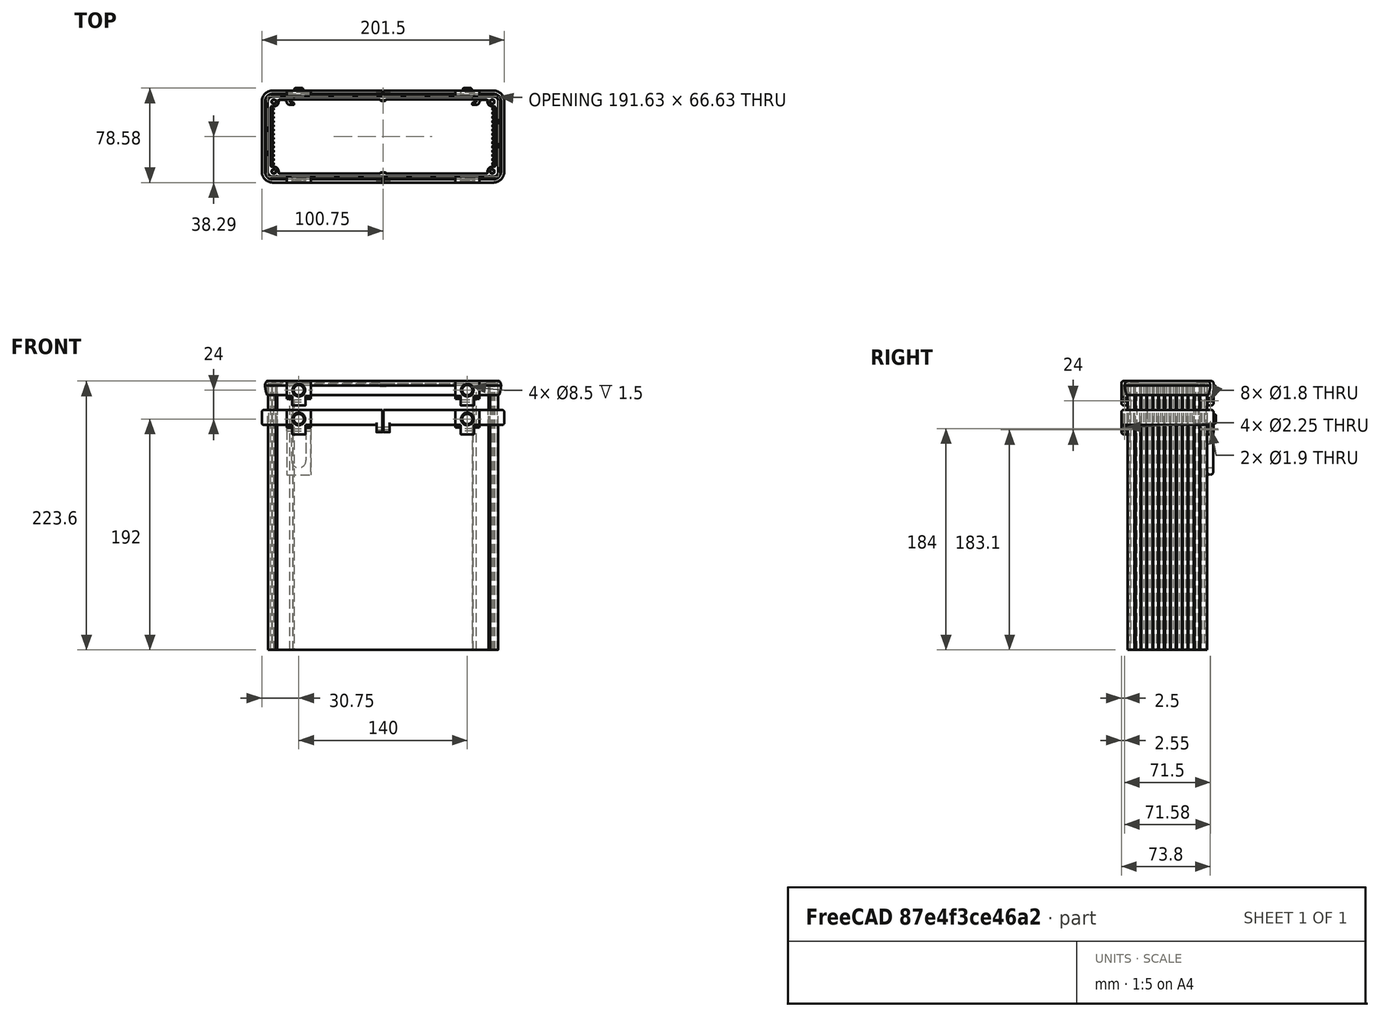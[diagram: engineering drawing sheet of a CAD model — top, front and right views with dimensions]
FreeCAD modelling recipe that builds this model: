
FCSTD DOCUMENT  (FreeCAD 1.0R38806 (Git))
Label: BevelHinge
License: All rights reserved
LicenseURL: http://en.wikipedia.org/wiki/All_rights_reserved
objects: PartDesign::Body×11, Sketcher::SketchObject×10, PartDesign::Pad×8, PartDesign::FeatureBase×6, PartDesign::Pocket×5, PartDesign::Fillet×4, Part::Feature×3, PartDesign::SubShapeBinder×3, App::Link×2, App::FeaturePython×2, Part::Compound×2, Mesh::Feature×1, Assembly::JointGroup×1, Assembly::AssemblyObject×1, PartDesign::Chamfer×1, Part::Mirroring×1
note: 106 computed .brp shape members not serialized (recipe doc carries the construction recipe); baked Part::Feature solids carry a one-line shape summary decoded from their .brp

FEATURE [Mesh::Feature] Lenovo_flip_feet_V3_2mm
FEATURE [Part::Feature] Lenovo_flip_feet_V3_2mm001
  Placement = pos=(-1.1e-15,-66.3,79.6) rot=(0,-0.707107,0.707107;3.14159rad)
  shape: bbox 20 x 5 x 43.92 mm, 906 faces, 0 solids (baked)
FEATURE [Part::Feature] Part__Feature019  label="1455U Open Bezel"
  Placement = pos=(6.2e-15,-33.01,110) rot=(0,0,1;0rad)
  shape: bbox 196.1 x 71.1 x 11.6 mm, 100 faces (baked)
FEATURE [Sketcher::SketchObject] Sketch
  ArcFitTolerance = 1e-06
  AttachmentSupport = -> [XZ_Plane]
  FullyConstrained = true
  MakeInternals = false
  MapMode = 5
  Placement = pos=(0,0,0) rot=(1,0,0;1.5708rad)
  sketch-geometry (11):
    g0: LineSegment StartX=-4.5 StartY=-1.2 StartZ=0 EndX=1.812e-13 EndY=-1.2 EndZ=0
    g1: LineSegment StartX=1.812e-13 StartY=-1.2 StartZ=0 EndX=1.812e-13 EndY=3.6 EndZ=0
    g2: LineSegment StartX=-4.5 StartY=-1.2 StartZ=0 EndX=-4.5 EndY=-6.7 EndZ=0
    g3: LineSegment StartX=-4.5 StartY=-6.7 StartZ=0 EndX=-15.5 EndY=-6.7 EndZ=0
    g4: LineSegment StartX=-15.5 StartY=-6.7 StartZ=0 EndX=-15.5 EndY=-1.2 EndZ=0
    g5: LineSegment StartX=-15.5 StartY=-1.2 StartZ=0 EndX=-20 EndY=-1.2 EndZ=0
    g6: LineSegment StartX=-20 StartY=-1.2 StartZ=0 EndX=-20 EndY=3.6 EndZ=0
    g7: ArcOfCircle [constr] CenterX=-10 CenterY=3.6 CenterZ=0 NormalX=0 NormalY=0 NormalZ=1 AngleXU=0 Radius=10 StartAngle=-2.64579e-11 EndAngle=3.14159
    g8: LineSegment StartX=-20 StartY=3.6 StartZ=0 EndX=-20 EndY=13.6 EndZ=0
    g9: LineSegment StartX=-20 StartY=13.6 StartZ=0 EndX=1.812e-13 EndY=13.6 EndZ=0
    g10: LineSegment StartX=1.812e-13 StartY=3.6 StartZ=0 EndX=1.812e-13 EndY=13.6 EndZ=0
  constraints (31):
    c: Horizontal(g0)
    c: Coincident(g0,g1)
    c: Vertical(g1)
    c: Coincident(g0,g2)
    c: Vertical(g2)
    c: Coincident(g2,g3)
    c: Horizontal(g3)
    c: Coincident(g3,g4)
    c: Vertical(g4)
    c: Coincident(g4,g5)
    c: Horizontal(g5)
    c: Coincident(g5,g6)
    c: Vertical(g6)
    c: Tangent(g7,g6) = 1.5708
    c: Tangent(g7,g1) = -1.5708
    c: DistanceX(g3,g3) = 11
    c: DistanceY(g4,g4) = 5.5
    c: Equal(g0,g5)
    c: DistanceX(g5,g5) = 4.5
    c: PointOnObject(g0,g-2)
    c: DistanceY(g0,g-1) = 1.2
    c: DistanceY(g6,g6) = 4.8
    c: Equal(g6,g1)
    c: Coincident(g8,g6)
    c: Vertical(g8)
    c: Horizontal(g9)
    c: Coincident(g10,g9)
    c: Vertical(g10)
    c: Coincident(g10,g1)
    c: Coincident(g8,g9)
    c: Tangent(g7,g9)
FEATURE [PartDesign::Pad] Pad
  Direction = (0,-1,2e-16)
  Length = 5
  Length2 = 10
  Placement = pos=(0,0,0) rot=(1,0,0;1.5708rad)
  Profile = -> Sketch
  ReferenceAxis = -> Sketch [N_Axis]
  Suppressed = false
  Type = 0
FEATURE [Sketcher::SketchObject] Sketch001
  ArcFitTolerance = 1e-06
  AttachmentSupport = -> [Pad]
  ExternalGeometry = -> [Pad]
  FullyConstrained = true
  MakeInternals = false
  MapMode = 5
  Placement = pos=(1.812e-13,0,0) rot=(0.707107,0,0.707107;3.14159rad)
  sketch-geometry (3):
    g0: LineSegment StartX=-1.2 StartY=0 StartZ=0 EndX=1 EndY=5 EndZ=0
    g1: LineSegment StartX=1 StartY=5 StartZ=0 EndX=-1.2 EndY=5 EndZ=0
    g2: LineSegment StartX=-1.2 StartY=5 StartZ=0 EndX=-1.2 EndY=0 EndZ=0
  constraints (8):
    c: Coincident(g0,g1)
    c: Horizontal(g1)
    c: Coincident(g1,g2)
    c: Vertical(g2)
    c: Coincident(g0,g2)
    c: Coincident(g0,g-3)
    c: PointOnObject(g0,g-4)
    c: DistanceX(g-1,g0) = 1
FEATURE [PartDesign::Pocket] Pocket
  BaseFeature = -> Pad
  Direction = (-1,0,2e-16)
  Length = 0
  Length2 = 5
  Placement = pos=(0,0,0) rot=(1,0,0;1.5708rad)
  Profile = -> Sketch001
  ReferenceAxis = -> Sketch001 [N_Axis]
  Suppressed = false
  Type = 3
  UpToFace = -> Pad [Face10]
FEATURE [PartDesign::SubShapeBinder] Binder
  BindCopyOnChange = 0
  BindMode = 0
  ClaimChildren = false
  Context = -> Body [Binder.]
  Fuse = false
  MakeFace = true
  OffsetFill = false
  OffsetIntersection = false
  OffsetJoinType = 0
  OffsetOpenResult = false
  PartialLoad = false
  Placement = pos=(-22,0,0) rot=(0,0,1;0rad)
  Relative = true
  Support = -> [Sketch001]
  _Version = 2
FEATURE [PartDesign::Pocket] Pocket001
  BaseFeature = -> Pocket
  Direction = (-1,0,2e-16)
  Length = 0
  Length2 = 5
  Placement = pos=(0,0,0) rot=(1,0,0;1.5708rad)
  Profile = -> Binder
  Reversed = true
  Suppressed = false
  Type = 3
  UpToFace = -> Pocket [Face7]
FEATURE [Sketcher::SketchObject] Sketch002
  ArcFitTolerance = 1e-06
  AttachmentSupport = -> [YZ_Plane]
  FullyConstrained = true
  MakeInternals = false
  MapMode = 5
  Placement = pos=(0,0,0) rot=(0.57735,0.57735,0.57735;2.0944rad)
  sketch-geometry (1):
    g0: Circle CenterX=-2.5 CenterY=-2.9 CenterZ=0 NormalX=0 NormalY=0 NormalZ=1 AngleXU=0 Radius=0.9
  constraints (3):
    c: DistanceX(g0) = -2.5
    c: DistanceY(g0) = -2.9
    c: Diameter(g0) = 1.8
FEATURE [PartDesign::Pocket] Pocket002
  BaseFeature = -> Pocket001
  Direction = (-1,0,0)
  Length = 5
  Length2 = 5
  Placement = pos=(0,0,0) rot=(1,0,0;1.5708rad)
  Profile = -> Sketch002
  ReferenceAxis = -> Sketch002 [N_Axis]
  Suppressed = false
  Type = 1
FEATURE [Sketcher::SketchObject] Sketch003
  ArcFitTolerance = 1e-06
  AttachmentSupport = -> [XZ_Plane001]
  FullyConstrained = true
  MakeInternals = false
  MapMode = 5
  Placement = pos=(0,0,0) rot=(1,0,0;1.5708rad)
  sketch-geometry (8):
    g0: LineSegment StartX=0 StartY=-0.5 StartZ=0 EndX=-4 EndY=-0.5 EndZ=0
    g1: LineSegment StartX=-4 StartY=-0.5 StartZ=0 EndX=-4 EndY=-28.5 EndZ=0
    g2: LineSegment StartX=-16 StartY=-28.5 StartZ=0 EndX=-16 EndY=-0.5 EndZ=0
    g3: LineSegment StartX=-16 StartY=-0.5 StartZ=0 EndX=-20 EndY=-0.5 EndZ=0
    g4: LineSegment StartX=-20 StartY=-0.5 StartZ=0 EndX=-20 EndY=-40.5 EndZ=0
    g5: LineSegment StartX=-20 StartY=-40.5 StartZ=0 EndX=0 EndY=-40.5 EndZ=0
    g6: LineSegment StartX=0 StartY=-40.5 StartZ=0 EndX=0 EndY=-0.5 EndZ=0
    g7: ArcOfCircle CenterX=-10 CenterY=-28.5 CenterZ=0 NormalX=0 NormalY=0 NormalZ=1 AngleXU=0 Radius=6 StartAngle=3.14159 EndAngle=6.28319
  constraints (23):
    c: Horizontal(g0)
    c: Coincident(g0,g1)
    c: Vertical(g1)
    c: Vertical(g2)
    c: Coincident(g2,g3)
    c: Horizontal(g3)
    c: Coincident(g3,g4)
    c: Vertical(g4)
    c: Coincident(g4,g5)
    c: PointOnObject(g5,g-2)
    c: Horizontal(g5)
    c: Coincident(g5,g6)
    c: Coincident(g6,g0)
    c: Vertical(g6)
    c: Tangent(g7,g1) = 1.5708
    c: Tangent(g7,g2) = 1.5708
    c: DistanceX(g3,g3) = 4
    c: Equal(g3,g0)
    c: Equal(g1,g2)
    c: DistanceY(g4,g4) = 40
    c: DistanceY(g2,g2) = 28
    c: DistanceX(g2,g0) = 12
    c: DistanceY(g0,g-1) = 0.5
FEATURE [PartDesign::Pad] Pad001
  Direction = (0,-1,2e-16)
  Length = 5
  Length2 = 10
  Placement = pos=(0,0,0) rot=(1,0,0;1.5708rad)
  Profile = -> Sketch003
  ReferenceAxis = -> Sketch003 [N_Axis]
  Suppressed = false
  Type = 0
FEATURE [Sketcher::SketchObject] Sketch004
  ArcFitTolerance = 1e-06
  AttachmentSupport = -> [YZ_Plane001]
  ExternalGeometry = -> [Pad001]
  FullyConstrained = true
  MakeInternals = false
  MapMode = 5
  Placement = pos=(0,0,0) rot=(0.57735,0.57735,0.57735;2.0944rad)
  sketch-geometry (11):
    g0: Circle CenterX=-2.5 CenterY=-2.9 CenterZ=0 NormalX=0 NormalY=0 NormalZ=1 AngleXU=0 Radius=0.95
    g1: ArcOfCircle CenterX=-2.5 CenterY=-37.8 CenterZ=0 NormalX=0 NormalY=0 NormalZ=1 AngleXU=0 Radius=2.5 StartAngle=3.14159 EndAngle=6.28319
    g2: LineSegment StartX=-5 StartY=-37.8 StartZ=0 EndX=-5 EndY=-2.4 EndZ=0
    g3: LineSegment StartX=-5 StartY=-2.4 StartZ=0 EndX=-3.1 EndY=-0.5 EndZ=0
    g4: ArcOfCircle CenterX=-3.09998 CenterY=-3.59998 CenterZ=0 NormalX=0 NormalY=0 NormalZ=1 AngleXU=0 Radius=3.09998 StartAngle=1e-16 EndAngle=1.5708
    g5: LineSegment StartX=-4e-16 StartY=-3.59998 StartZ=0 EndX=-4e-16 EndY=-37.8 EndZ=0
    g6: LineSegment [constr] StartX=-2.5 StartY=-37.8 StartZ=0 EndX=-2.5 EndY=-40.3 EndZ=0
    g7: LineSegment StartX=-10 StartY=5 StartZ=0 EndX=-10 EndY=-45 EndZ=0
    g8: LineSegment StartX=-10 StartY=-45 StartZ=0 EndX=10 EndY=-45 EndZ=0
    g9: LineSegment StartX=10 StartY=-45 StartZ=0 EndX=10 EndY=5 EndZ=0
    g10: LineSegment StartX=10 StartY=5 StartZ=0 EndX=-10 EndY=5 EndZ=0
  constraints (31):
    c: DistanceX(g0) = -2.5
    c: DistanceY(g0) = -2.9
    c: Diameter(g0) = 1.9
    c: Vertical(g2)
    c: Tangent(g2,g1) = 1.5708
    c: Coincident(g3,g4)
    c: Coincident(g3,g2)
    c: Vertical(g5)
    c: Tangent(g1,g5) = 1.5708
    c: Tangent(g5,g4) = 1.5708
    c: PointOnObject(g4,g-2)
    c: DistanceX(g2,g-1) = 5
    c: PointOnObject(g3,g-3)
    c: DistanceX(g2,g3) = 1.9
    c: Tangent(g4,g-3)
    c: Coincident(g6,g1)
    c: PointOnObject(g6,g1)
    c: Vertical(g6)
    c: DistanceY(g6) = -40.3
    c: DistanceY(g2) = -2.4
    c: Coincident(g7,g8)
    c: Coincident(g8,g9)
    c: Coincident(g9,g10)
    c: Coincident(g10,g7)
    c: Vertical(g7)
    c: Vertical(g9)
    c: Horizontal(g8)
    c: Symmetric(g7,g9,g-2)
    c: DistanceY(g7,g7) = 50
    c: DistanceX(g10,g10) = 20
    c: DistanceY(g9) = 5
FEATURE [App::Link] Body002
  LinkPlacement = pos=(3.99107,-60.6985,90.648) rot=(0,0,1;0rad)
  LinkedObject = -> Body
  Placement = pos=(3.99107,-60.6985,90.648) rot=(0,0,1;0rad)
FEATURE [App::FeaturePython] GroundedJoint  # Assembly grounded joint (typed FeaturePython)
  ObjectToGround = -> Body002
  Placement = pos=(3.99107,-60.6985,90.648) rot=(0,0,1;0rad)
FEATURE [App::Link] Body003
  LinkPlacement = pos=(1.73898,-284.407,480.336) rot=(0.999747,0.013661,0.017877;4.13204rad)
  LinkedObject = -> Body001
  Placement = pos=(1.73898,-284.407,480.336) rot=(0.999747,0.013661,0.017877;4.13204rad)
FEATURE [PartDesign::Pocket] Pocket003
  BaseFeature = -> Pad001
  Direction = (-1,0,0)
  Length = 5
  Length2 = 5
  Placement = pos=(0,0,0) rot=(1,0,0;1.5708rad)
  Profile = -> Sketch004
  ReferenceAxis = -> Sketch004 [N_Axis]
  Suppressed = false
  Type = 1
FEATURE [PartDesign::Body] Body001  label="Hinge"
  AllowCompound = false
  Group = -> [Sketch003,Pad001,Sketch004,Pocket003]
  Origin = -> Origin001
  Placement = pos=(-60,5,76) rot=(0,0,1;0rad)
  Tip = -> Pocket003
FEATURE [PartDesign::Fillet] Fillet
  Base = -> Pocket002 [Edge26,Edge20]
  BaseFeature = -> Pocket002
  Placement = pos=(0,0,0) rot=(1,0,0;1.5708rad)
  Radius = 2
  SupportTransform = false
  Suppressed = false
  UseAllEdges = false
FEATURE [App::FeaturePython] Revolute  # Assembly joint (typed FeaturePython)
  Activated = true
  AngleMax = 0
  AngleMin = -113.85
  Detach1 = false
  Detach2 = false
  Distance = 0
  Distance2 = 0
  EnableAngleMax = true
  EnableAngleMin = true
  EnableLengthMax = false
  EnableLengthMin = false
  JointType = 1 (Revolute)
  LengthMax = 0
  LengthMin = 0
  Placement1 = pos=(-2.25,-5,1) rot=(-0.707107,0,0.707107;3.14159rad)
  Placement2 = pos=(-13.8391,204.961,395.868) rot=(-0.999798,-0.012245,-0.015925;4.1597rad)
  Reference1 = -> Assembly [Body002.Fillet.Edge6,Body002.Fillet.Edge6]
  Reference2 = -> Assembly [Body003.Pocket003.?Edge31,Body003.Pocket003.?Edge31]
FEATURE [Assembly::JointGroup] Joints
  Group = -> [GroundedJoint,Revolute]
FEATURE [Assembly::AssemblyObject] Assembly
  Group = -> [Joints,Body002,GroundedJoint,Body003,Revolute]
  Origin = -> Origin002
  Type = Assembly
FEATURE [Sketcher::SketchObject] Sketch005
  ArcFitTolerance = 1e-06
  AttachmentOffset = pos=(0,0,2.5) rot=(0,0,1;0rad)
  AttachmentSupport = -> [XZ_Plane]
  FullyConstrained = true
  MakeInternals = false
  MapMode = 5
  Placement = pos=(0,-2.5,6e-16) rot=(1,0,0;1.5708rad)
  sketch-geometry (1):
    g0: Circle CenterX=-10 CenterY=6 CenterZ=0 NormalX=0 NormalY=0 NormalZ=1 AngleXU=0 Radius=4.25
  constraints (3):
    c: DistanceX(g0,g-1) = 10
    c: DistanceY(g0,g-1) = -6
    c: Diameter(g0) = 8.5
FEATURE [PartDesign::Pocket] Pocket004
  BaseFeature = -> Fillet
  Direction = (0,1,-2e-16)
  Length = 5
  Length2 = 5
  Placement = pos=(0,0,0) rot=(1,0,0;1.5708rad)
  Profile = -> Sketch005
  ReferenceAxis = -> Sketch005 [N_Axis]
  Reversed = true
  Suppressed = false
  Type = 0
FEATURE [PartDesign::FeatureBase] Clone001
  BaseFeature = -> Fillet
  Placement = pos=(0,0,0) rot=(1,0,0;1.5708rad)
  Suppressed = false
FEATURE [Sketcher::SketchObject] Sketch006
  ArcFitTolerance = 1e-06
  AttachmentOffset = pos=(0,0,5) rot=(0,0,1;0rad)
  AttachmentSupport = -> [XZ_Plane004]
  FullyConstrained = true
  MakeInternals = false
  MapMode = 5
  Placement = pos=(0,-5,1.1e-15) rot=(1,0,0;1.5708rad)
  sketch-geometry (1):
    g0: Circle CenterX=-10 CenterY=6 CenterZ=0 NormalX=0 NormalY=0 NormalZ=1 AngleXU=0 Radius=3.75
  constraints (3):
    c: DistanceX(g0) = -10
    c: DistanceY(g0) = 6
    c: Diameter(g0) = 7.5
FEATURE [PartDesign::Pad] Pad002
  BaseFeature = -> Clone001
  Direction = (0,-1,2e-16)
  Length = 2
  Length2 = 10
  Placement = pos=(0,0,0) rot=(1,0,0;1.5708rad)
  Profile = -> Sketch006
  ReferenceAxis = -> Sketch006 [N_Axis]
  Suppressed = false
  Type = 0
FEATURE [PartDesign::Fillet] Fillet001
  Base = -> Pad002 [Face19]
  BaseFeature = -> Pad002
  Placement = pos=(0,0,0) rot=(1,0,0;1.5708rad)
  Radius = 1
  SupportTransform = false
  Suppressed = false
  UseAllEdges = false
FEATURE [PartDesign::Body] Body005
  AllowCompound = false
  Group = -> [Clone001,Sketch006,Pad002,Fillet001]
  Origin = -> Origin004
  Placement = pos=(-80,0.28,100) rot=(0,0,1;3.14159rad)
  Tip = -> Fillet001
FEATURE [PartDesign::Chamfer] Chamfer
  Angle = 45
  Base = -> Pocket004 [Edge18]
  BaseFeature = -> Pocket004
  ChamferType = 0
  FlipDirection = false
  Placement = pos=(0,0,0) rot=(1,0,0;1.5708rad)
  Size = 1
  Size2 = 1
  SupportTransform = false
  Suppressed = false
  UseAllEdges = false
FEATURE [PartDesign::Body] Body
  AllowCompound = false
  Group = -> [Sketch,Pad,Sketch001,Pocket,Binder,Pocket001,Sketch002,Pocket002,Fillet,Sketch005,Pocket004,Chamfer]
  Origin = -> Origin
  Placement = pos=(-60,-66.3,100) rot=(0,0,1;0rad)
  Tip = -> Chamfer
FEATURE [PartDesign::FeatureBase] Clone
  BaseFeature = -> Body
  Placement = pos=(-60,-66.3,100) rot=(0,0,1;0rad)
  Suppressed = false
FEATURE [PartDesign::Body] Body004
  AllowCompound = false
  Group = -> [Clone]
  Origin = -> Origin003
  Placement = pos=(140,0,0) rot=(0,0,1;0rad)
  Tip = -> Clone
FEATURE [PartDesign::FeatureBase] Clone002
  BaseFeature = -> Body005
  Placement = pos=(-80,0.28,100) rot=(0,0,1;3.14159rad)
  Suppressed = false
FEATURE [PartDesign::Body] Body006
  AllowCompound = false
  Group = -> [Clone002]
  Origin = -> Origin005
  Placement = pos=(140,0,0) rot=(0,0,1;0rad)
  Tip = -> Clone002
FEATURE [Part::Compound] Compound
  Links = -> [Part__Feature019,Body,Body004,Body005,Body006]
FEATURE [PartDesign::FeatureBase] Clone003
  BaseFeature = -> Body
  Placement = pos=(-60,-66.3,100) rot=(0,0,1;0rad)
  Suppressed = false
FEATURE [PartDesign::Body] Body007
  AllowCompound = false
  Group = -> [Clone003]
  Origin = -> Origin006
  Placement = pos=(0,0,-14) rot=(0,0,1;0rad)
  Tip = -> Clone003
FEATURE [PartDesign::FeatureBase] Clone004
  BaseFeature = -> Body005
  Placement = pos=(-80,0.28,100) rot=(0,0,1;3.14159rad)
  Suppressed = false
FEATURE [PartDesign::Body] Body008
  AllowCompound = false
  Group = -> [Clone004]
  Origin = -> Origin007
  Placement = pos=(0,0,-14) rot=(0,0,1;0rad)
  Tip = -> Clone004
FEATURE [Part::Feature] Part__Feature017  label="U extrusion 220mm"
  Placement = pos=(-8e-15,-66,0) rot=(0,0,1;3.14159rad)
  shape: bbox 191 x 66 x 220 mm, 418 faces (baked)
FEATURE [Sketcher::SketchObject] Sketch007
  ArcFitTolerance = 1e-06
  AttachmentSupport = -> [XY_Plane008]
  FullyConstrained = true
  MakeInternals = false
  MapMode = 5
  sketch-geometry (13):
    g0: ArcOfCircle CenterX=-91.5 CenterY=-4 CenterZ=0 NormalX=0 NormalY=0 NormalZ=1 AngleXU=0 Radius=4.25 StartAngle=1.5708 EndAngle=3.14159
    g1: ArcOfCircle CenterX=-91.5 CenterY=-62 CenterZ=0 NormalX=0 NormalY=0 NormalZ=1 AngleXU=0 Radius=4.25 StartAngle=3.14159 EndAngle=4.71239
    g2: ArcOfCircle CenterX=-91.5 CenterY=-4 CenterZ=0 NormalX=0 NormalY=0 NormalZ=1 AngleXU=0 Radius=9.25 StartAngle=1.5708 EndAngle=3.14159
    g3: ArcOfCircle CenterX=-91.5 CenterY=-62 CenterZ=0 NormalX=0 NormalY=0 NormalZ=1 AngleXU=0 Radius=9.25 StartAngle=3.14159 EndAngle=4.7124
    g4: LineSegment StartX=-91.5 StartY=0.25 StartZ=0 EndX=-76 EndY=0.25 EndZ=0
    g5: LineSegment StartX=-91.5 StartY=5.25 StartZ=0 EndX=-76 EndY=5.25 EndZ=0
    g6: LineSegment StartX=-76 StartY=5.25 StartZ=0 EndX=-76 EndY=0.25 EndZ=0
    g7: LineSegment StartX=-91.5 StartY=-66.25 StartZ=0 EndX=-75.9999 EndY=-66.25 EndZ=0
    g8: LineSegment StartX=-91.4999 StartY=-71.25 StartZ=0 EndX=-75.9999 EndY=-71.25 EndZ=0
    g9: LineSegment StartX=-75.9999 StartY=-66.25 StartZ=0 EndX=-75.9999 EndY=-71.25 EndZ=0
    g10: LineSegment StartX=-100.75 StartY=-4 StartZ=0 EndX=-100.75 EndY=-62 EndZ=0
    g11: LineSegment StartX=-95.75 StartY=-4 StartZ=0 EndX=-95.75 EndY=-62 EndZ=0
    g12: LineSegment [constr] StartX=-76 StartY=0.25 StartZ=0 EndX=-76 EndY=0 EndZ=0
  constraints (34):
    c: Coincident(g2,g0)
    c: Coincident(g3,g1)
    c: Horizontal(g4)
    c: Horizontal(g5)
    c: Coincident(g6,g5)
    c: Coincident(g6,g4)
    c: Horizontal(g7)
    c: Coincident(g8,g3)
    c: Horizontal(g8)
    c: Coincident(g9,g7)
    c: Coincident(g9,g8)
    c: Vertical(g10)
    c: Vertical(g11)
    c: Vertical(g6)
    c: Vertical(g9)
    c: Equal(g8,g5)
    c: Equal(g9,g6)
    c: Tangent(g11,g0) = -1.5708
    c: Tangent(g10,g2) = -1.5708
    c: Tangent(g10,g3) = -1.5708
    c: Tangent(g11,g1) = -1.5708
    c: Equal(g1,g0)
    c: Tangent(g4,g0) = 1.5708
    c: DistanceY(g6,g6) = 5
    c: Coincident(g12,g4)
    c: Vertical(g12)
    c: PointOnObject(g12,g-1)
    c: DistanceY(g12,g12) = 0.25
    c: Tangent(g5,g2) = 1.5708
    c: DistanceX(g5,g5) = 15.5
    c: DistanceX(g12) = -76
    c: Radius(g0) = 4.25
    c: Tangent(g7,g1) = -1.5708
    c: DistanceY(g10,g10) = 58
FEATURE [PartDesign::Pad] Pad003
  Direction = (0,0,1)
  Length = 12.6
  Length2 = 10
  Profile = -> Sketch007
  ReferenceAxis = -> Sketch007 [N_Axis]
  Suppressed = false
  Type = 0
FEATURE [PartDesign::Fillet] Fillet002
  Base = -> Pad003 [Edge28]
  BaseFeature = -> Pad003
  Radius = 2
  SupportTransform = false
  Suppressed = false
  UseAllEdges = false
FEATURE [PartDesign::Fillet] Fillet003
  Base = -> Fillet002 [Edge18]
  BaseFeature = -> Fillet002
  Radius = 2
  SupportTransform = false
  Suppressed = false
  UseAllEdges = false
FEATURE [PartDesign::Body] Body009
  AllowCompound = false
  Group = -> [Sketch007,Pad003,Fillet002,Fillet003]
  Origin = -> Origin008
  Placement = pos=(0,0,87) rot=(0,0,1;0rad)
  Tip = -> Fillet003
FEATURE [PartDesign::SubShapeBinder] Binder002
  BindCopyOnChange = 0
  BindMode = 0
  ClaimChildren = false
  Context = -> Body012 [Binder002.]
  Fuse = false
  MakeFace = true
  OffsetFill = false
  OffsetIntersection = false
  OffsetJoinType = 0
  OffsetOpenResult = false
  PartialLoad = false
  Placement = pos=(16,0,0) rot=(0,0,1;0rad)
  Relative = true
  Support = -> [Body009[Fillet003.Face21]]
  _Version = 2
FEATURE [PartDesign::Pad] Pad005
  Direction = (1,0,0)
  Length = 59.5
  Length2 = 10
  Placement = pos=(16,0,0) rot=(0,0,1;0rad)
  Profile = -> Binder002
  Suppressed = false
  Type = 0
FEATURE [Sketcher::SketchObject] Sketch008
  ArcFitTolerance = 1e-06
  AttachmentSupport = -> [Pad005]
  ExternalGeometry = -> [Pad005]
  FullyConstrained = true
  MakeInternals = false
  MapMode = 5
  Placement = pos=(-0.49994,0,0) rot=(0.57735,0.57735,0.57735;2.0944rad)
  sketch-geometry (6):
    g0: Circle CenterX=-68.75 CenterY=84 CenterZ=0 NormalX=0 NormalY=0 NormalZ=1 AngleXU=0 Radius=1.125
    g1: LineSegment StartX=-71.25 StartY=89 StartZ=0 EndX=-66.25 EndY=87 EndZ=0
    g2: LineSegment StartX=-66.25 StartY=87 StartZ=0 EndX=-66.25 EndY=81 EndZ=0
    g3: LineSegment StartX=-71.25 StartY=89 StartZ=0 EndX=-71.25 EndY=83 EndZ=0
    g4: ArcOfCircle CenterX=-69.25 CenterY=83 CenterZ=0 NormalX=0 NormalY=0 NormalZ=1 AngleXU=0 Radius=2 StartAngle=3.14159 EndAngle=4.71239
    g5: LineSegment StartX=-69.25 StartY=81 StartZ=0 EndX=-66.25 EndY=81 EndZ=0
  constraints (15):
    c: Diameter(g0) = 2.25  'holeDia'
    c: Coincident(g2,g-4)
    c: Vertical(g2)
    c: Coincident(g3,g-3)
    c: Vertical(g3)
    c: Horizontal(g5)
    c: Coincident(g2,g5)
    c: Tangent(g4,g5) = -1.5708
    c: Tangent(g4,g3) = -1.5708
    c: Coincident(g1,g3)
    c: Coincident(g1,g2)
    c: DistanceX(g0,g2) = 2.5
    c: DistanceY(g0,g1) = 3
    c: DistanceY(g4,g0) = 3
    c: Equal(g4,g-5)
FEATURE [PartDesign::Pad] Pad006
  BaseFeature = -> Pad005
  Direction = (1,0,0)
  Length = 5
  Length2 = 10
  Placement = pos=(16,0,0) rot=(0,0,1;0rad)
  Profile = -> Sketch008
  ReferenceAxis = -> Sketch008 [N_Axis]
  Reversed = true
  Suppressed = false
  Type = 0
FEATURE [PartDesign::Body] Body012
  AllowCompound = false
  Group = -> [Binder002,Pad005,Sketch008,Pad006]
  Origin = -> Origin011
  Tip = -> Pad006
FEATURE [PartDesign::SubShapeBinder] Binder003
  BindCopyOnChange = 0
  BindMode = 0
  ClaimChildren = false
  Context = -> Body011 [Binder003.]
  Fuse = false
  MakeFace = true
  OffsetFill = false
  OffsetIntersection = false
  OffsetJoinType = 0
  OffsetOpenResult = false
  PartialLoad = false
  Placement = pos=(16,0,0) rot=(0,0,1;0rad)
  Relative = true
  Support = -> [Body009[Fillet003.Face5]]
  _Version = 2
FEATURE [PartDesign::Pad] Pad004
  Direction = (1,0,0)
  Length = 59.5
  Length2 = 10
  Placement = pos=(16,0,0) rot=(0,0,1;0rad)
  Profile = -> Binder003
  Suppressed = false
  Type = 0
FEATURE [Sketcher::SketchObject] Sketch009
  ArcFitTolerance = 1e-06
  AttachmentSupport = -> [Pad004]
  ExternalGeometry = -> [Pad004]
  FullyConstrained = true
  MakeInternals = false
  MapMode = 5
  Placement = pos=(-0.5,0,0) rot=(0.57735,0.57735,0.57735;2.0944rad)
  sketch-geometry (6):
    g0: LineSegment StartX=0.25 StartY=87 StartZ=0 EndX=0.25 EndY=81 EndZ=0
    g1: LineSegment StartX=0.25 StartY=81 StartZ=0 EndX=3.25 EndY=81 EndZ=0
    g2: LineSegment StartX=5.25 StartY=89 StartZ=0 EndX=5.25 EndY=83 EndZ=0
    g3: ArcOfCircle CenterX=3.25 CenterY=83 CenterZ=0 NormalX=0 NormalY=0 NormalZ=1 AngleXU=0 Radius=2 StartAngle=4.71239 EndAngle=6.28319
    g4: Circle CenterX=2.75 CenterY=84 CenterZ=0 NormalX=0 NormalY=0 NormalZ=1 AngleXU=0 Radius=1.125
    g5: LineSegment StartX=0.25 StartY=87 StartZ=0 EndX=5.25 EndY=89 EndZ=0
  constraints (15):
    c: Coincident(g0,g-3)
    c: Vertical(g0)
    c: Coincident(g1,g0)
    c: Horizontal(g1)
    c: Tangent(g2,g3) = 1.5708
    c: Coincident(g2,g-4)
    c: Vertical(g2)
    c: Tangent(g3,g1) = -1.5708
    c: DistanceX(g0,g4) = 2.5
    c: DistanceY(g4,g0) = 3
    c: DistanceY(g1,g4) = 3
    c: Equal(g3,g-4)
    c: Coincident(g5,g0)
    c: Coincident(g5,g2)
    c: Diameter(g4) = 2.25
FEATURE [PartDesign::Pad] Pad007
  BaseFeature = -> Pad004
  Direction = (1,0,0)
  Length = 5
  Length2 = 10
  Placement = pos=(16,0,0) rot=(0,0,1;0rad)
  Profile = -> Sketch009
  ReferenceAxis = -> Sketch009 [N_Axis]
  Reversed = true
  Suppressed = false
  Type = 0
FEATURE [PartDesign::Body] Body011
  AllowCompound = false
  Group = -> [Pad004,Binder003,Sketch009,Pad007]
  Origin = -> Origin010
  Tip = -> Pad007
FEATURE [Part::Compound] Compound001  label="Bevel"
  Links = -> [Body007,Body008,Body009,Body011,Body012]
  Placement = pos=(0,0,-10) rot=(0,0,1;0rad)
FEATURE [PartDesign::FeatureBase] Clone005
  BaseFeature = -> Compound001
  Placement = pos=(0,0,-10) rot=(0,0,1;0rad)
  Suppressed = false
FEATURE [PartDesign::Body] Body010
  AllowCompound = false
  Group = -> [Clone005]
  Origin = -> Origin009
  Tip = -> Clone005
FEATURE [Part::Mirroring] Part__Mirroring  label="BevelMirror"
  Base = (0,0,0)
  Normal = (1,0,0)
  Source = -> Clone005
